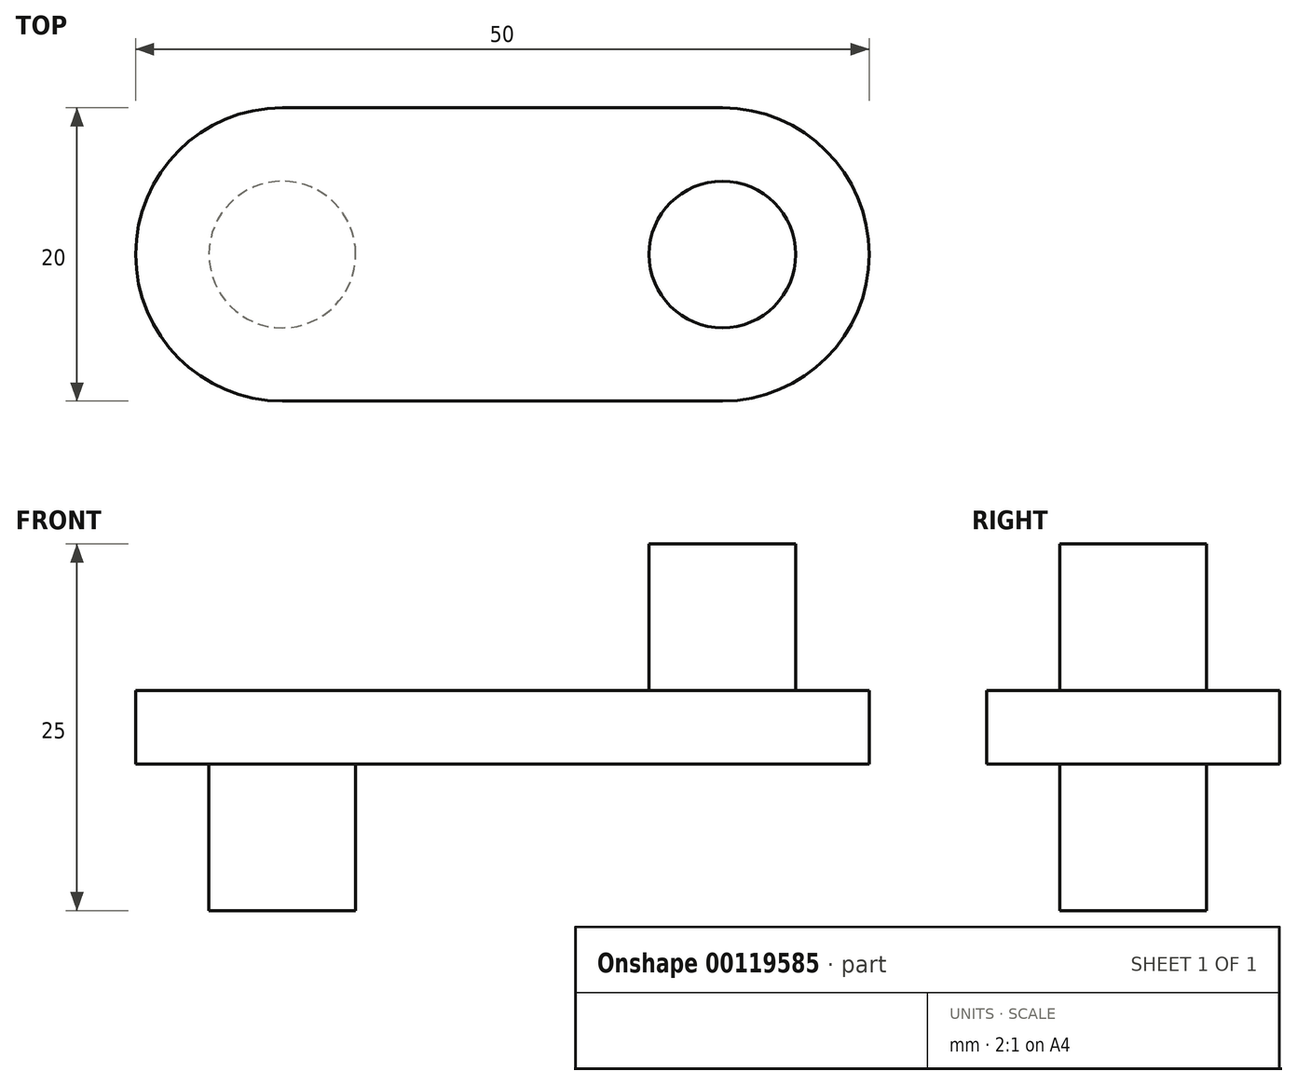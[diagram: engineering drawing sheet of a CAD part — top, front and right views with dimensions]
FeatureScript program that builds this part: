
annotation { "Feature Type Name" : "Feature", "Feature Type Description" : "" }
export const myFeature = defineFeature(function(context is Context, id is Id, definition is map)
    precondition{}
    {
        {
            var Q0;
            Q0=qCreatedBy(makeId("Top.planeOp"),FACE);
            var sketch = newSketch(context, id + "F0", { "sketchPlane" : qUnion([Q0])});
            skLineSegment(sketch, "E0.bottom", {"start": v(-58.8, 0.05) * mm, "end": v(61.2, 0.05) * mm});
            skLineSegment(sketch, "E0.top", {"start": v(-58.8, -39.95) * mm, "end": v(61.2, -39.95) * mm});
            skLineSegment(sketch, "E0.left", {"start": v(-58.8, 0.05) * mm, "end": v(-58.8, -39.95) * mm});
            skLineSegment(sketch, "E0.right", {"start": v(61.2, 0.05) * mm, "end": v(61.2, -39.95) * mm});
            skCircle(sketch, "E1", {"center": v(-38.8, -19.95) * mm, "radius": 5 * mm});
            skCircle(sketch, "E2", {"center": v(41.2, -19.95) * mm, "radius": 5 * mm});
            skSolve(sketch);
        }
        {
            var Q0;
            Q0=makeQuery(id+"F0.imprint","IMPRINT",FACE,{"disambiguationData":[TD([[makeQuery(id+"F0.imprint","IMPRINT",EDGE,{"derivedFrom":sQuery(id+"F0.wireOp",EDGE,"E0.bottom")}),-1.0]])]});
            extrude(context, id + "F1", {"entities" : qUnion([Q0]), "depth" : 15 * mm});
        }
        {
            var Q0;
            Q0=qCreatedBy(makeId("Top.planeOp"),FACE);
            var sketch = newSketch(context, id + "F2", { "sketchPlane" : qUnion([Q0])});
            skLineSegment(sketch, "E3.bottom", {"start": v(-16.1, 28.13) * mm, "end": v(13.9, 28.13) * mm});
            skLineSegment(sketch, "E3.top", {"start": v(-16.1, 8.13) * mm, "end": v(13.9, 8.13) * mm});
            skLineSegment(sketch, "E3.left", {"start": v(-16.1, 28.13) * mm, "end": v(-16.1, 8.13) * mm});
            skLineSegment(sketch, "E3.right", {"start": v(13.9, 28.13) * mm, "end": v(13.9, 8.13) * mm});
            skArc(sketch, "E4", {"start": v(13.9, 8.13) * mm, "mid": v(23.9, 18.13) * mm, "end": v(13.9, 28.13) * mm});
            skArc(sketch, "E5", {"start": v(-16.1, 28.13) * mm, "mid": v(-26.1, 18.13) * mm, "end": v(-16.1, 8.13) * mm});
            skSolve(sketch);
        }
        {
            var Q0;
            Q0 = qSketchRegion(id + "F2", true);
            extrude(context, id + "F3", {"entities" : qUnion([Q0]), "depth" : 5 * mm});
        }
        {
            var Q0;
            Q0=makeQuery(id+"F3.opExtrude","CAP_FACE",FACE,{"disambiguationData":[OSD([sQuery(id+"F2.wireOp",EDGE,"E3.bottom"),sQuery(id+"F2.wireOp",EDGE,"E3.top"),sQuery(id+"F2.wireOp",EDGE,"E4"),sQuery(id+"F2.wireOp",EDGE,"E5")])],"isStart":true});
            var sketch = newSketch(context, id + "F4", { "sketchPlane" : qUnion([Q0])});
            skCircle(sketch, "E6", {"center": v(-16.1, -18.13) * mm, "radius": 5 * mm});
            skSolve(sketch);
        }
        {
            var Q0;
            Q0 = qSketchRegion(id + "F4", true);
            extrude(context, id + "F5", {"entities" : qUnion([Q0]), "operationType" : NewBodyOperationType.ADD, "depth" : 10 * mm});
        }
        {
            var Q0;
            Q0=qCreatedBy(makeId("Top.planeOp"),FACE);
            var sketch = newSketch(context, id + "F6", { "sketchPlane" : qUnion([Q0])});
            skCircle(sketch, "E7", {"center": v(13.9, 18.13) * mm, "radius": 5 * mm});
            skSolve(sketch);
        }
        {
            var Q0;
            Q0 = qSketchRegion(id + "F6", true);
            extrude(context, id + "F7", {"entities" : qUnion([Q0]), "operationType" : NewBodyOperationType.ADD, "depth" : 15 * mm});
        }
        {
            var Q0;
            Q0=makeQuery(id+"F1.opExtrude","SWEPT_BODY",BODY,{"disambiguationData":[OSD([sQuery(id+"F0.wireOp",EDGE,"E0.bottom"),sQuery(id+"F0.wireOp",EDGE,"E0.top"),sQuery(id+"F0.wireOp",EDGE,"E0.left"),sQuery(id+"F0.wireOp",EDGE,"E0.right"),sQuery(id+"F0.wireOp",EDGE,"E1"),sQuery(id+"F0.wireOp",EDGE,"E2")])]});
            deleteBodies(context, id + "F8", {"entities" : qUnion([Q0])});
        }
    });
